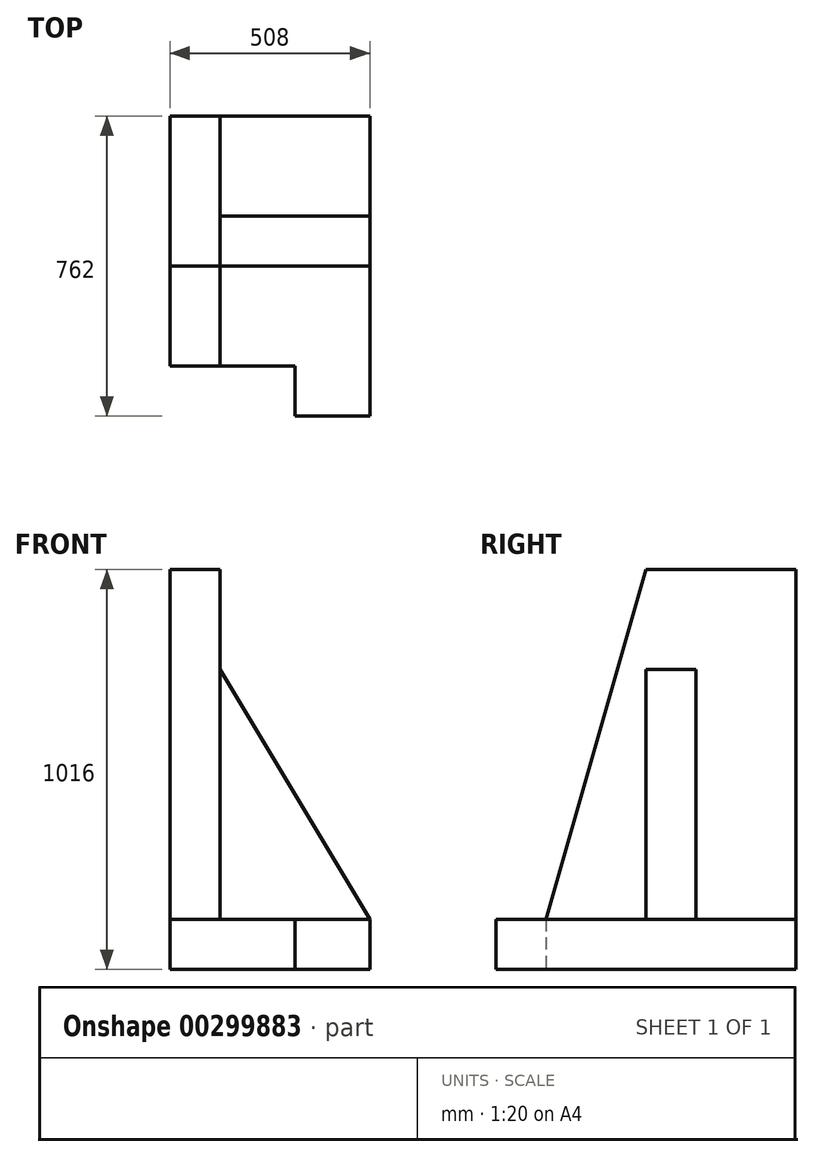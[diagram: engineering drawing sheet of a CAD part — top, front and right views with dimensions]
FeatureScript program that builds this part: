
annotation { "Feature Type Name" : "Feature", "Feature Type Description" : "" }
export const myFeature = defineFeature(function(context is Context, id is Id, definition is map)
    precondition{}
    {
        {
            var Q0;
            Q0=qCreatedBy(makeId("Top.planeOp"),FACE);
            var sketch = newSketch(context, id + "F0", { "sketchPlane" : qUnion([Q0])});
            skLineSegment(sketch, "E0.bottom", {"start": v(0, 254) * mm, "end": v(508, 254) * mm});
            skLineSegment(sketch, "E0.right", {"start": v(508, 254) * mm, "end": v(508, -508) * mm});
            skLineSegment(sketch, "E1", {"start": v(508, -508) * mm, "end": v(317.5, -508) * mm});
            skLineSegment(sketch, "E2", {"start": v(317.5, -508) * mm, "end": v(317.5, -381) * mm});
            skLineSegment(sketch, "E3", {"start": v(317.5, -381) * mm, "end": v(0, -381) * mm});
            skLineSegment(sketch, "E4", {"start": v(0, -381) * mm, "end": v(0, 254) * mm});
            skSolve(sketch);
        }
        {
            var Q0;
            Q0 = qSketchRegion(id + "F0", true);
            extrude(context, id + "F1", {"entities" : qUnion([Q0]), "depth" : 127 * mm});
        }
        {
            var Q0;
            Q0=makeQuery(id+"F1.opExtrude","SWEPT_FACE",FACE,{"disambiguationData":[OSD([sQuery(id+"F0.wireOp",EDGE,"E4")])]});
            var sketch = newSketch(context, id + "F2", { "sketchPlane" : qUnion([Q0])});
            skLineSegment(sketch, "E5", {"start": v(-254, 127) * mm, "end": v(-254, 1016) * mm});
            skLineSegment(sketch, "E6", {"start": v(-254, 1016) * mm, "end": v(127, 1016) * mm});
            skLineSegment(sketch, "E7", {"start": v(127, 1016) * mm, "end": v(381, 127) * mm});
            skLineSegment(sketch, "E8", {"start": v(381, 127) * mm, "end": v(-254, 127) * mm});
            skSolve(sketch);
        }
        {
            var Q0;
            Q0 = qSketchRegion(id + "F2", true);
            extrude(context, id + "F3", {"entities" : qUnion([Q0]), "operationType" : NewBodyOperationType.ADD, "oppositeDirection" : true, "depth" : 127 * mm});
        }
        {
            var Q0;
            Q0=makeQuery(id+"F3.boolean.opBoolean","MERGE",FACE,{"derivedFrom":[makeQuery(id+"F1.opExtrude","SWEPT_FACE",FACE,{"disambiguationData":[OSD([sQuery(id+"F0.wireOp",EDGE,"E0.bottom")])]}),makeQuery(id+"F3.opExtrude","SWEPT_FACE",FACE,{"disambiguationData":[OSD([sQuery(id+"F2.wireOp",EDGE,"E5")])]})]});
            var sketch = newSketch(context, id + "F4", { "sketchPlane" : qUnion([Q0])});
            skLineSegment(sketch, "E9", {"start": v(-127, 127) * mm, "end": v(-127, 762) * mm});
            skLineSegment(sketch, "E10", {"start": v(-127, 762) * mm, "end": v(-508, 127) * mm});
            skLineSegment(sketch, "E11", {"start": v(-508, 127) * mm, "end": v(-127, 127) * mm});
            skSolve(sketch);
        }
        {
            var Q0;
            Q0 = qSketchRegion(id + "F4", true);
            extrude(context, id + "F5", {"entities" : qUnion([Q0]), "operationType" : NewBodyOperationType.ADD, "oppositeDirection" : true, "depth" : 381 * mm});
        }
        {
            var Q0;
            Q0 = qSketchRegion(id + "F4", true);
            extrude(context, id + "F6", {"entities" : qUnion([Q0]), "operationType" : NewBodyOperationType.REMOVE, "oppositeDirection" : true, "depth" : 254 * mm});
        }
    });
